# Revit family: BVN_BDTX
name_source: partatom
category: Mechanical Equipment
units: mm (PartAtom-declared; Revit-internal decimal feet)

## family parameters
Always vertical = Yes
Cut with Voids When Loaded = No
OmniClass Number = 23.75.00.00
OmniClass Title = Climate Control (HVAC)
Part Type = Breaks Into
Room Calculation Point = No
Round Connector Dimension = Use Diameter
Shared = No
Work Plane-Based = No

## types (12) — shared parameters
Description = Duct Fan
Frequency = 50 Hz
Manufacturer = Bahçıvan Elektrik Motor San. ve Tic. Ltd. Şti.
Material = <By Category>
Model = BDTX
Protection Class = 44
URL = http://www.bahcivanmotor.com.tr
Voltage = 230 V

## per-type parameters (varying)
| type | Air Flow | BDTX 100 | BDTX 125 | BDTX 150 | BDTX 160 | BDTX 200A | BDTX 250A | BDTX 315A | BDTX 355 | Capacitor | Current | D | Insulation Class | Power | Q | Sound Pressure Level dB(A) | Speed ( d/d ) | Weight |
| BDTX 100 | 275.0 m³/h | Yes | No | No | No | No | No | No | No | 2 | 0 A | 197 mm | B | 60 W | 100 mm  [stored 0.328084 ft] | 44 | 2960 | 2.60 kg |
| BDTX 125 | 315.0 m³/h | No | Yes | No | No | No | No | No | No | 2.5 | 0 A | 188 mm | B | 80 W | 125 mm | 43 | 2325 | 2.70 kg |
| BDTX 150 | 420.0 m³/h | No | No | Yes | No | No | No | No | No | 2.5 | 0 A | 192 mm | B | 78 W | 150 mm | 46 | 2450 | 3.00 kg |
| BDTX 160 | 440.0 m³/h | No | No | No | Yes | No | No | No | No | 2.5 | 0 A | 192 mm | B | 85 W | 160 mm | 45 | 2550 | 3.20 kg |
| BDTX 200A | 735.0 m³/h | No | No | No | No | Yes | No | No | No | 2.5 | 0 A | 230 mm | B | 90 W | 200 mm | 46 | 2300 | 4.40 kg |
| BDTX 200B | 935.0 m³/h | No | No | No | No | Yes | No | No | No | 4 | 1 A | 230 mm | B | 130 W | 200 mm | 48 | 2720 | 4.80 kg |
| BDTX 250A | 1010.0 m³/h | No | No | No | No | No | Yes | No | No | 4 | 1 A | 227 mm | B | 140 W | 250 mm  [stored 0.82021 ft] | 45 | 2400 | 4.90 kg |
| BDTX 250B | 1150.0 m³/h | No | No | No | No | No | Yes | No | No | 6 | 1 A | 227 mm | B | 200 W | 250 mm  [stored 0.82021 ft] | 47 | 2650 | 5.30 kg |
| BDTX 315A | 1450.0 m³/h | No | No | No | No | No | No | Yes | No | 6 | 1 A | 285 mm | B | 210 W | 315 mm | 48 | 2400 | 6.80 kg |
| BDTX 315B | 1890.0 m³/h | No | No | No | No | No | No | Yes | No | 7 | 1 A | 285 mm | B | 245 W | 315 mm | 49 | 2700 | 6.90 kg |
| BDTX 355-A | 1530.0 m³/h | No | No | No | No | No | No | No | Yes | 3 | 1 A | 378 mm  [stored 1.24016 ft] | F | 165 W | 355 mm | 45 | 1650 | 9.00 kg |
| BDTX 355-B | 2620.0 m³/h | No | No | No | No | No | No | No | Yes | 8 | 2 A | 378 mm  [stored 1.24016 ft] | F | 445 W | 355 mm | 54 | 2450 | 9.00 kg |

note: [stored X ft] marks values corroborated as IEEE doubles in the binary element streams (Revit-internal decimal feet)

## geometry (parser evidence)
native form markers: Sweep x2
no freeform markers — native parametric forms only
